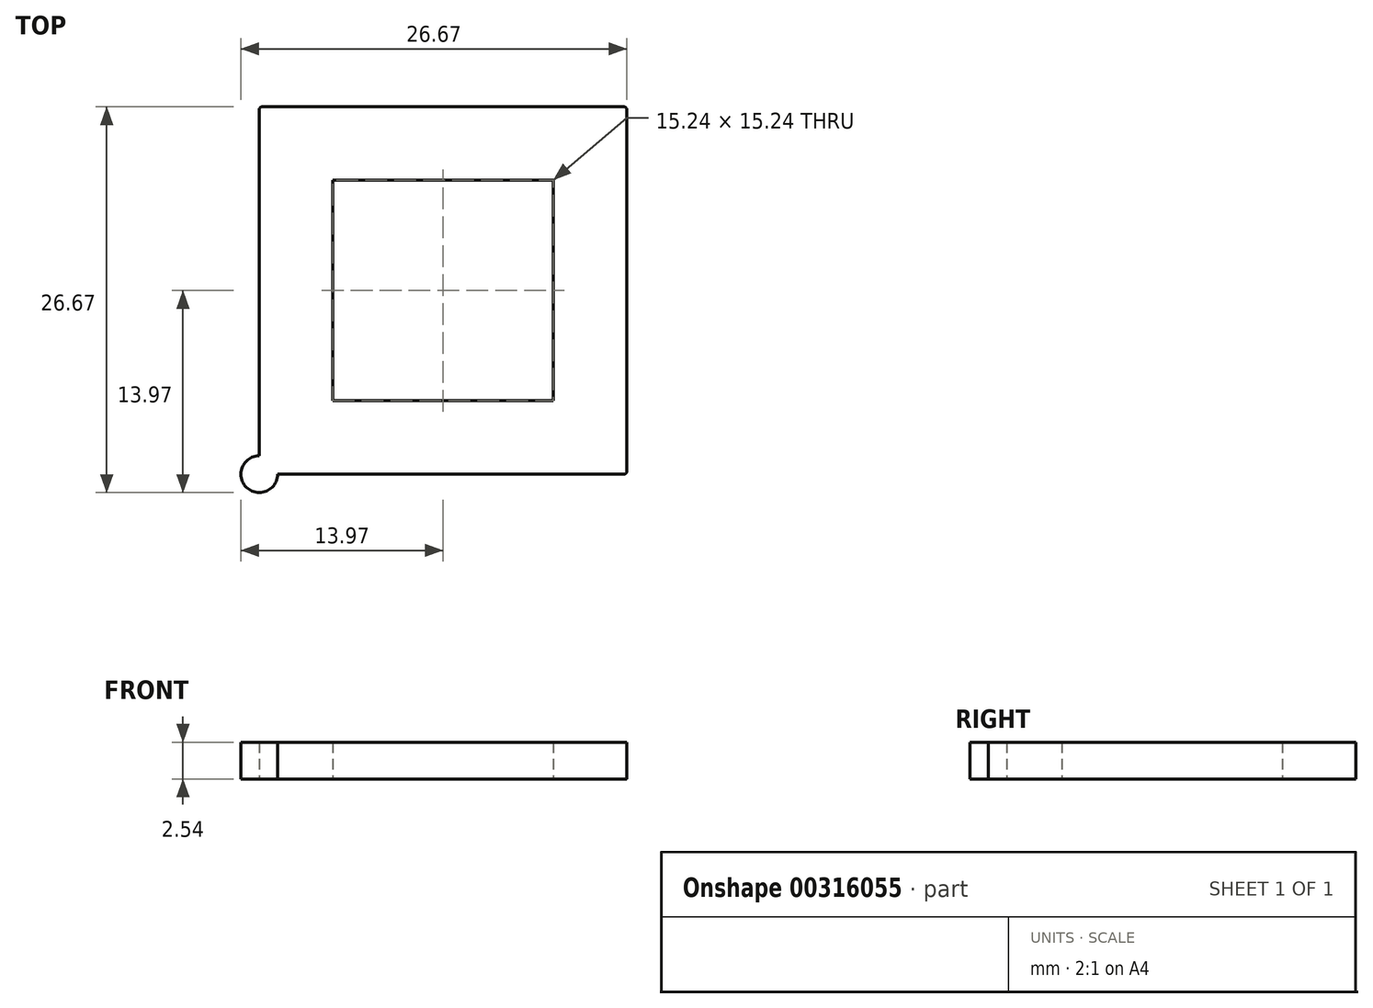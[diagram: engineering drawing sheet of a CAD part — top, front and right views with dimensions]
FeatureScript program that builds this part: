
annotation { "Feature Type Name" : "Feature", "Feature Type Description" : "" }
export const myFeature = defineFeature(function(context is Context, id is Id, definition is map)
    precondition{}
    {
        {
            var Q0;
            Q0=qCreatedBy(makeId("Top.planeOp"),FACE);
            var sketch = newSketch(context, id + "F0", { "sketchPlane" : qUnion([Q0])});
            skLineSegment(sketch, "E0.bottom", {"start": v(12.5, -12.7) * mm, "end": v(-11.43, -12.7) * mm});
            skLineSegment(sketch, "E0.top", {"start": v(12.5, 12.7) * mm, "end": v(-12.5, 12.7) * mm});
            skLineSegment(sketch, "E0.left", {"start": v(12.7, -12.5) * mm, "end": v(12.7, 12.5) * mm});
            skLineSegment(sketch, "E0.right", {"start": v(-12.7, -11.43) * mm, "end": v(-12.7, 12.5) * mm});
            skPoint(sketch, "E0.middle", {"position": v(0, 0) * mm});
            skLineSegment(sketch, "E1.0", {"start": v(-7.62, -7.62) * mm, "end": v(-7.62, 7.62) * mm});
            skLineSegment(sketch, "E1.1", {"start": v(7.62, -7.62) * mm, "end": v(-7.62, -7.62) * mm});
            skLineSegment(sketch, "E1.2", {"start": v(7.62, -7.62) * mm, "end": v(7.62, 7.62) * mm});
            skLineSegment(sketch, "E1.3", {"start": v(7.62, 7.62) * mm, "end": v(-7.62, 7.62) * mm});
            skPoint(sketch, "E2.visualSharp", {"position": v(-12.7, 12.7) * mm});
            skArc(sketch, "E2.filletArc", {"start": v(-12.5, 12.7) * mm, "mid": v(-12.64, 12.64) * mm, "end": v(-12.7, 12.5) * mm});
            skPoint(sketch, "E3.visualSharp", {"position": v(12.7, 12.7) * mm});
            skArc(sketch, "E3.filletArc", {"start": v(12.7, 12.5) * mm, "mid": v(12.64, 12.64) * mm, "end": v(12.5, 12.7) * mm});
            skPoint(sketch, "E4.visualSharp", {"position": v(12.7, -12.7) * mm});
            skArc(sketch, "E4.filletArc", {"start": v(12.5, -12.7) * mm, "mid": v(12.64, -12.64) * mm, "end": v(12.7, -12.5) * mm});
            skArc(sketch, "E5", {"start": v(-12.7, -11.43) * mm, "mid": v(-13.6, -13.6) * mm, "end": v(-11.43, -12.7) * mm});
            skSolve(sketch);
        }
        {
            var Q0;
            Q0=qSketchRegion(id+"F0",true);
            extrude(context, id + "F1", {"entities" : qUnion([Q0]), "depth" : 2.54 * mm});
        }
    });
